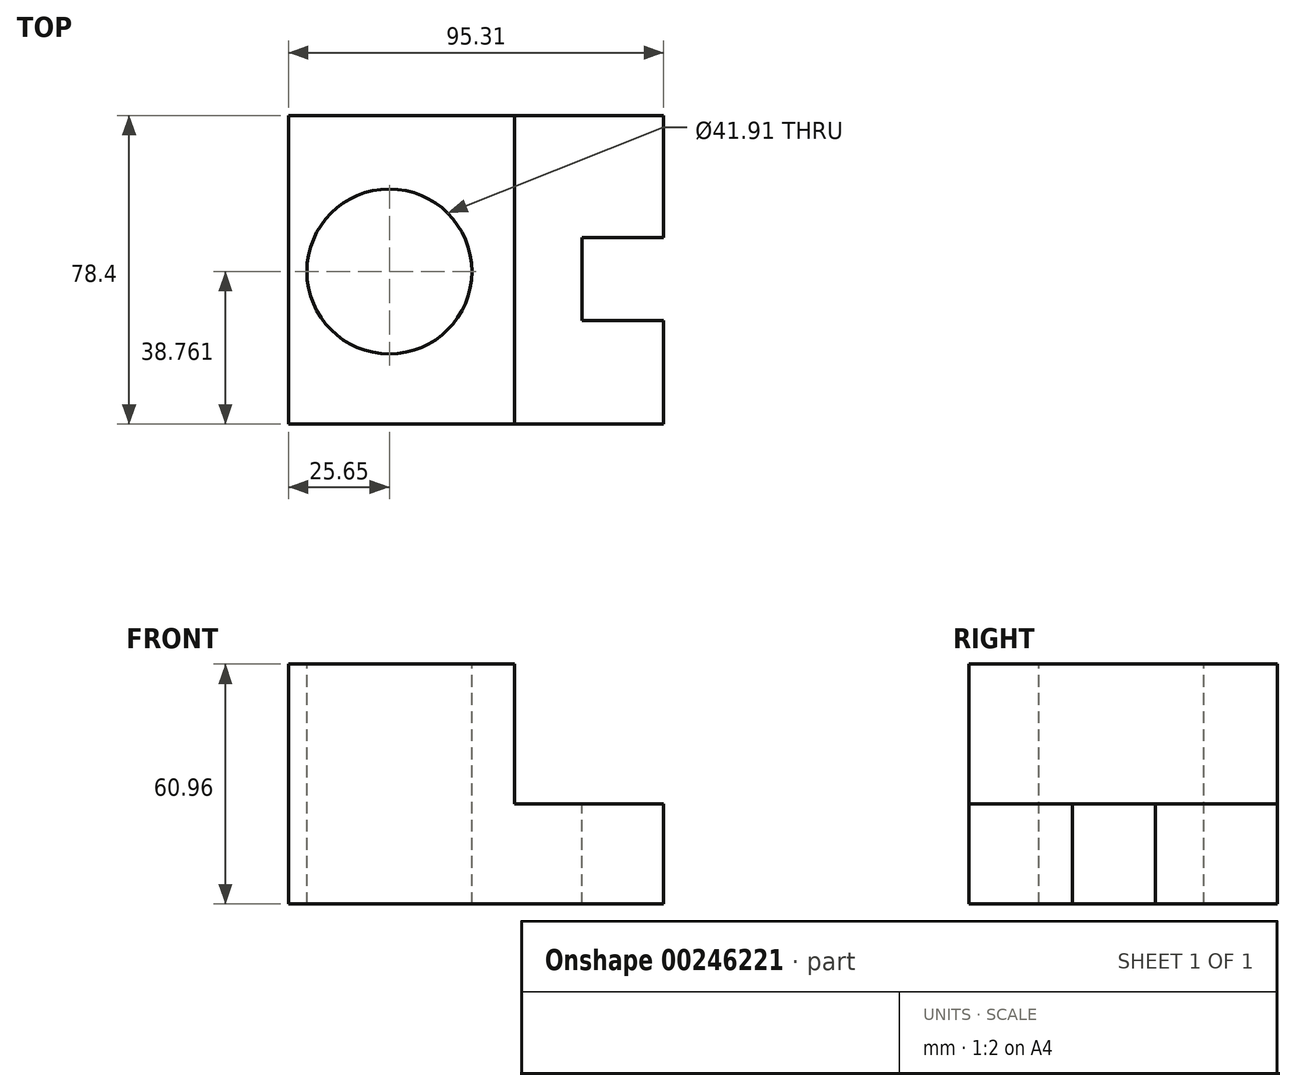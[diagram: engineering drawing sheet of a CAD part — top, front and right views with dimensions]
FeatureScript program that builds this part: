
annotation { "Feature Type Name" : "Feature", "Feature Type Description" : "" }
export const myFeature = defineFeature(function(context is Context, id is Id, definition is map)
    precondition{}
    {
        {
            var Q0;
            Q0=qCreatedBy(makeId("Top.planeOp"),FACE);
            var sketch = newSketch(context, id + "F0", { "sketchPlane" : qUnion([Q0])});
            skLineSegment(sketch, "E0.bottom", {"start": v(-35.56, 31.04) * mm, "end": v(59.75, 31.04) * mm});
            skLineSegment(sketch, "E0.top", {"start": v(-35.56, -47.36) * mm, "end": v(59.75, -47.36) * mm});
            skLineSegment(sketch, "E0.left", {"start": v(-35.56, 31.04) * mm, "end": v(-35.56, -47.36) * mm});
            skLineSegment(sketch, "E0.right", {"start": v(59.75, 31.04) * mm, "end": v(59.75, -47.36) * mm});
            skSolve(sketch);
        }
        {
            var Q0;
            Q0=makeQuery(id+"F0.imprint","IMPRINT",FACE,{"disambiguationData":[TD([[makeQuery(id+"F0.imprint","IMPRINT",EDGE,{"derivedFrom":sQuery(id+"F0.wireOp",EDGE,"E0.bottom")}),-1.0]])]});
            extrude(context, id + "F1", {"entities" : qUnion([Q0]), "depth" : 25.4 * mm});
        }
        {
            var Q0;
            Q0=makeQuery(id+"F1.opExtrude","CAP_FACE",FACE,{"disambiguationData":[OSD([sQuery(id+"F0.wireOp",EDGE,"E0.bottom"),sQuery(id+"F0.wireOp",EDGE,"E0.top"),sQuery(id+"F0.wireOp",EDGE,"E0.left"),sQuery(id+"F0.wireOp",EDGE,"E0.right")])],"isStart":false});
            var sketch = newSketch(context, id + "F2", { "sketchPlane" : qUnion([Q0])});
            skLineSegment(sketch, "E1.bottom", {"start": v(59.75, 0) * mm, "end": v(39.06, 0) * mm});
            skLineSegment(sketch, "E1.top", {"start": v(59.75, -21.07) * mm, "end": v(39.06, -21.07) * mm});
            skLineSegment(sketch, "E1.left", {"start": v(59.75, 0) * mm, "end": v(59.75, -21.07) * mm});
            skLineSegment(sketch, "E1.right", {"start": v(39.06, 0) * mm, "end": v(39.06, -21.07) * mm});
            skSolve(sketch);
        }
        {
            var Q0;
            Q0=makeQuery(id+"F2.imprint","IMPRINT",FACE,{"disambiguationData":[TD([[makeQuery(id+"F2.imprint","IMPRINT",EDGE,{"derivedFrom":sQuery(id+"F2.wireOp",EDGE,"E1.bottom")}),1.0]])]});
            extrude(context, id + "F3", {"entities" : qUnion([Q0]), "operationType" : NewBodyOperationType.REMOVE, "oppositeDirection" : true, "depth" : 25.4 * mm});
        }
        {
            var Q0;
            Q0=makeQuery(id+"F1.opExtrude","CAP_FACE",FACE,{"disambiguationData":[OSD([sQuery(id+"F0.wireOp",EDGE,"E0.bottom"),sQuery(id+"F0.wireOp",EDGE,"E0.top"),sQuery(id+"F0.wireOp",EDGE,"E0.left"),sQuery(id+"F0.wireOp",EDGE,"E0.right")])],"isStart":false});
            var sketch = newSketch(context, id + "F4", { "sketchPlane" : qUnion([Q0])});
            skLineSegment(sketch, "E2.bottom", {"start": v(-35.56, 31.04) * mm, "end": v(21.86, 31.04) * mm});
            skLineSegment(sketch, "E2.top", {"start": v(-35.56, -47.36) * mm, "end": v(21.86, -47.36) * mm});
            skLineSegment(sketch, "E2.left", {"start": v(-35.56, 31.04) * mm, "end": v(-35.56, -47.36) * mm});
            skLineSegment(sketch, "E2.right", {"start": v(21.86, 31.04) * mm, "end": v(21.86, -47.36) * mm});
            skSolve(sketch);
        }
        {
            var Q0;
            Q0=makeQuery(id+"F4.imprint","IMPRINT",FACE,{"disambiguationData":[TD([[makeQuery(id+"F4.imprint","IMPRINT",EDGE,{"derivedFrom":sQuery(id+"F4.wireOp",EDGE,"E2.bottom")}),-1.0]])]});
            extrude(context, id + "F5", {"entities" : qUnion([Q0]), "operationType" : NewBodyOperationType.ADD, "depth" : 35.56 * mm});
        }
        {
            var Q0;
            Q0=makeQuery(id+"F5.opExtrude","CAP_FACE",FACE,{"disambiguationData":[OSD([sQuery(id+"F4.wireOp",EDGE,"E2.bottom"),sQuery(id+"F4.wireOp",EDGE,"E2.top"),sQuery(id+"F4.wireOp",EDGE,"E2.left"),sQuery(id+"F4.wireOp",EDGE,"E2.right")])],"isStart":false});
            var sketch = newSketch(context, id + "F6", { "sketchPlane" : qUnion([Q0])});
            skCircle(sketch, "E3", {"center": v(-9.62, -8.6) * mm, "radius": 20.86 * mm});
            skSolve(sketch);
        }
        {
            var Q0;
            Q0=makeQuery(id+"F6.imprint","IMPRINT",FACE,{"disambiguationData":[TD([[makeQuery(id+"F6.imprint","IMPRINT",EDGE,{"derivedFrom":sQuery(id+"F6.wireOp",EDGE,"E3")}),1.0]])]});
            var sketch = newSketch(context, id + "F7", { "sketchPlane" : qUnion([Q0])});
            skLineSegment(sketch, "E4", {"start": v(-9.91, -8.6) * mm, "end": v(74.62, -8.6) * mm});
            skLineSegment(sketch, "E5", {"start": v(-9.91, -8.6) * mm, "end": v(-12.82, 40.08) * mm});
            skLineSegment(sketch, "E6", {"start": v(-9.91, -8.6) * mm, "end": v(-55.67, -5.1) * mm});
            skLineSegment(sketch, "E7", {"start": v(-9.91, -8.6) * mm, "end": v(-7.73, -44.95) * mm});
            skSolve(sketch);
        }
        {
            var Q0;
            Q0=sQuery(id+"F7.wireOp",VERTEX,"E7.start");
            var Q1;
            Q1=makeQuery(id+"F1.opExtrude","SWEPT_BODY",BODY,{"disambiguationData":[OSD([sQuery(id+"F0.wireOp",EDGE,"E0.bottom"),sQuery(id+"F0.wireOp",EDGE,"E0.top"),sQuery(id+"F0.wireOp",EDGE,"E0.left"),sQuery(id+"F0.wireOp",EDGE,"E0.right")])]});
            hole(context, id + "F8", {"style" : HoleStyle.SIMPLE, "endStyle" : HoleEndStyle.THROUGH, "holeDiameter" : 41.9 * mm, "tappedDepth" : 12.7 * mm, "tapClearance" : 3, "locations" : qUnion([Q0]), "scope" : qUnion([Q1])});
        }
    });
